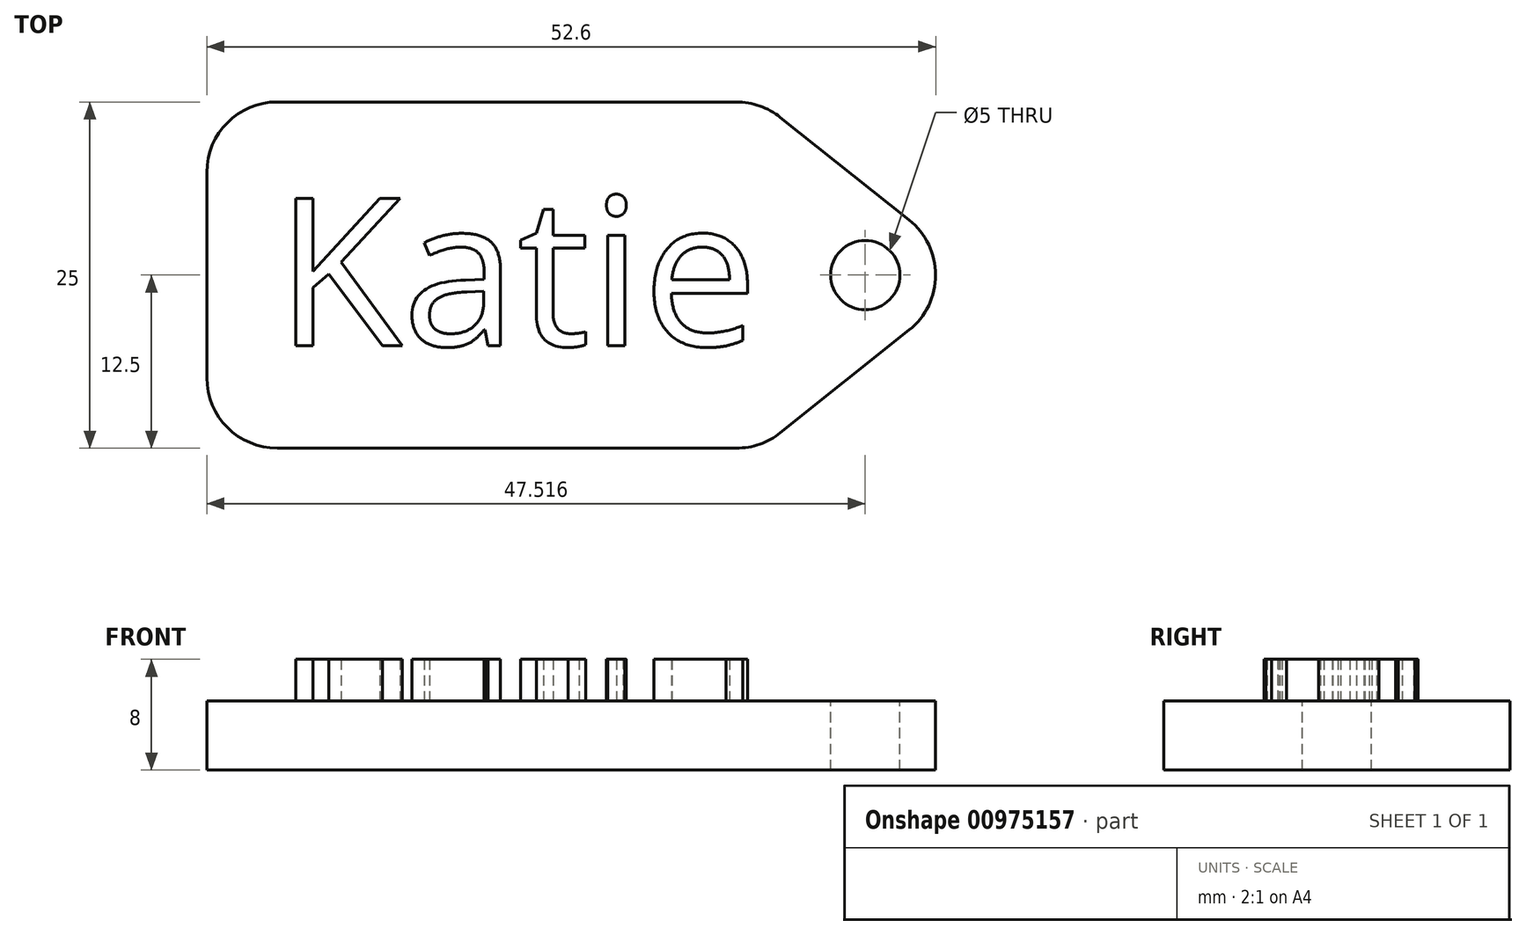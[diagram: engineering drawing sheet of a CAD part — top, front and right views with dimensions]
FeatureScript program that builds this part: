
annotation { "Feature Type Name" : "Feature", "Feature Type Description" : "" }
export const myFeature = defineFeature(function(context is Context, id is Id, definition is map)
    precondition{}
    {
        {
            var Q0;
            Q0=qCreatedBy(makeId("Top.planeOp"),FACE);
            var sketch = newSketch(context, id + "F0", { "sketchPlane" : qUnion([Q0])});
            skLineSegment(sketch, "E0.bottom", {"start": v(20, -12.5) * mm, "end": v(-20, -12.5) * mm});
            skLineSegment(sketch, "E0.top", {"start": v(20, 12.5) * mm, "end": v(-20, 12.5) * mm});
            skLineSegment(sketch, "E0.right", {"start": v(-20, -12.5) * mm, "end": v(-20, 12.5) * mm});
            skPoint(sketch, "E0.middle", {"position": v(0, 0) * mm});
            skPoint(sketch, "E1", {"position": v(35.66, 0) * mm});
            skLineSegment(sketch, "E2", {"start": v(20, 12.5) * mm, "end": v(35.66, 0) * mm});
            skLineSegment(sketch, "E3", {"start": v(20, -12.5) * mm, "end": v(35.66, 0) * mm});
            skSolve(sketch);
        }
        {
            var Q0;
            Q0 = qSketchRegion(id + "F0", true);
            extrude(context, id + "F1", {"entities" : qUnion([Q0]), "depth" : 5 * mm, "offsetDistance" : 25.4 * mm});
        }
        {
            var Q0;
            Q0=makeQuery(id+"F1.opExtrude","SWEPT_EDGE",EDGE,{"disambiguationData":[OSD([sQuery(id+"F0.wireOp",EDGE,"E2"),sQuery(id+"F0.wireOp",EDGE,"E3")])]});
            fillet(context, id + "F2", {"entities" : qUnion([Q0]), "radius" : 5.08 * mm, "tangentPropagation" : true, "allowEdgeOverflow" : false});
        }
        {
            var Q0;
            Q0=makeQuery(id+"F1.opExtrude","SWEPT_EDGE",EDGE,{"disambiguationData":[OSD([sQuery(id+"F0.wireOp",EDGE,"E0.bottom"),sQuery(id+"F0.wireOp",EDGE,"E3")])]});
            var Q1;
            Q1=makeQuery(id+"F1.opExtrude","SWEPT_EDGE",EDGE,{"disambiguationData":[OSD([sQuery(id+"F0.wireOp",EDGE,"E0.bottom"),sQuery(id+"F0.wireOp",EDGE,"E0.right")])]});
            var Q2;
            Q2=makeQuery(id+"F1.opExtrude","SWEPT_EDGE",EDGE,{"disambiguationData":[OSD([sQuery(id+"F0.wireOp",EDGE,"E0.top"),sQuery(id+"F0.wireOp",EDGE,"E0.right")])]});
            var Q3;
            Q3=makeQuery(id+"F1.opExtrude","SWEPT_EDGE",EDGE,{"disambiguationData":[OSD([sQuery(id+"F0.wireOp",EDGE,"E0.top"),sQuery(id+"F0.wireOp",EDGE,"E2")])]});
            fillet(context, id + "F3", {"entities" : qUnion([Q0, Q1, Q2, Q3]), "radius" : 5.08 * mm, "tangentPropagation" : true, "allowEdgeOverflow" : false});
        }
        {
            var Q0;
            Q0=makeQuery(id+"F1.opExtrude","CAP_FACE",FACE,{"disambiguationData":[OSD([sQuery(id+"F0.wireOp",EDGE,"E0.bottom"),sQuery(id+"F0.wireOp",EDGE,"E0.top"),sQuery(id+"F0.wireOp",EDGE,"E0.right"),sQuery(id+"F0.wireOp",EDGE,"E2"),sQuery(id+"F0.wireOp",EDGE,"E3")])],"isStart":false});
            var sketch = newSketch(context, id + "F4", { "sketchPlane" : qUnion([Q0])});
            skPoint(sketch, "E4", {"position": v(27.52, 0) * mm});
            skSolve(sketch);
        }
        {
            var Q0;
            Q0=sQuery(id+"F4.wireOp",VERTEX,"E4");
            var Q1;
            Q1=makeQuery(id+"F1.opExtrude","SWEPT_BODY",BODY,{"disambiguationData":[OSD([sQuery(id+"F0.wireOp",EDGE,"E0.bottom"),sQuery(id+"F0.wireOp",EDGE,"E0.top"),sQuery(id+"F0.wireOp",EDGE,"E0.right"),sQuery(id+"F0.wireOp",EDGE,"E2"),sQuery(id+"F0.wireOp",EDGE,"E3")])]});
            hole(context, id + "F5", {"style" : HoleStyle.SIMPLE, "endStyle" : HoleEndStyle.THROUGH, "holeDiameter" : 5 * mm, "majorDiameter" : 6.35 * mm, "isTappedThrough" : true, "tappedDepth" : 12.7 * mm, "tapClearance" : 3, "locations" : qUnion([Q0]), "scope" : qUnion([Q1])});
        }
        {
            var Q0;
            Q0=makeQuery(id+"F1.opExtrude","CAP_FACE",FACE,{"disambiguationData":[OSD([sQuery(id+"F0.wireOp",EDGE,"E0.bottom"),sQuery(id+"F0.wireOp",EDGE,"E0.top"),sQuery(id+"F0.wireOp",EDGE,"E0.right"),sQuery(id+"F0.wireOp",EDGE,"E2"),sQuery(id+"F0.wireOp",EDGE,"E3")])],"isStart":false});
            var sketch = newSketch(context, id + "F6", { "sketchPlane" : qUnion([Q0])});
            skText(sketch, "E5", { "text": "Katie", "fontName": "OpenSans-Regular.ttf"});
            const initialGuessF6  = {"E5": [-0.01503, -0.00509, 1, 0, 0.01073]};
            skSetInitialGuess(sketch, initialGuessF6);
            skSolve(sketch);
        }
        {
            var Q0;
            Q0 = qSketchRegion(id + "F6", true);
            extrude(context, id + "F7", {"entities" : qUnion([Q0]), "operationType" : NewBodyOperationType.ADD, "depth" : 3 * mm, "offsetDistance" : 25.4 * mm});
        }
    });
